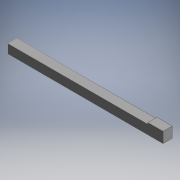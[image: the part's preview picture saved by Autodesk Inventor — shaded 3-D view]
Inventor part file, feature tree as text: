
AUTODESK INVENTOR PART (.ipt)
format: ipt  version: 2018 (Build 220112000, 112)  size: 118,784 bytes
history: native  units: in
note: dims shown in document units (in); Inventor stores cm internally (conversion verified against a paired STEP export)
features: extrude x2, other x2
ambient origin geometry x8: Origin, YZ Plane, XZ Plane, XY Plane, X Axis, Y Axis, Z Axis, Center Point
bodies: Body1 (feature_tree)
feature tree (4):
  extrude  "Tube"  Depth=0.3937in
  extrude  "Extrusion6"  Depth=0.3937in
  other  "Tube Base Sketch"
  other  "Cap Sketch"
